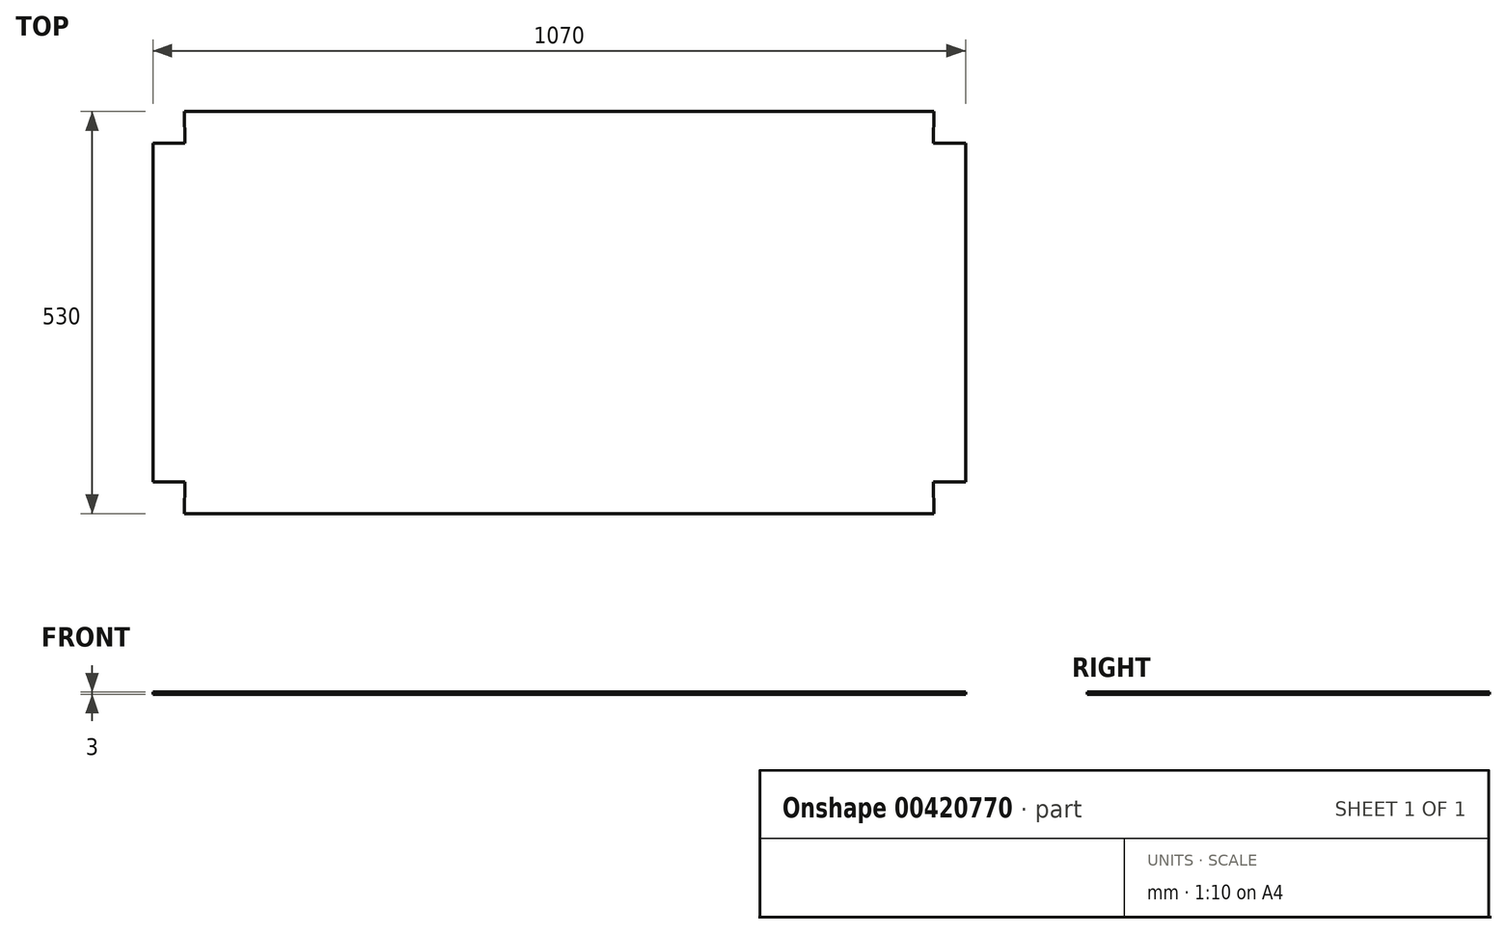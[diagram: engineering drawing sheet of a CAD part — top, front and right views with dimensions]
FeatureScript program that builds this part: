
annotation { "Feature Type Name" : "Feature", "Feature Type Description" : "" }
export const myFeature = defineFeature(function(context is Context, id is Id, definition is map)
    precondition{}
    {
        {
            var Q0;
            Q0=qCreatedBy(makeId("Top.planeOp"),FACE);
            var sketch = newSketch(context, id + "F0", { "sketchPlane" : qUnion([Q0])});
            skLineSegment(sketch, "E0.bottom", {"start": v(-882.96, -57.33) * mm, "end": v(104.05, -57.33) * mm});
            skLineSegment(sketch, "E0.top", {"start": v(-882.96, -587.33) * mm, "end": v(104.05, -587.33) * mm});
            skLineSegment(sketch, "E0.left", {"start": v(-924.45, -99.33) * mm, "end": v(-924.45, -545.33) * mm});
            skLineSegment(sketch, "E0.right", {"start": v(145.55, -99.33) * mm, "end": v(145.55, -545.33) * mm});
            skLineSegment(sketch, "E1.top", {"start": v(-924.45, -99.33) * mm, "end": v(-882.45, -99.33) * mm});
            skLineSegment(sketch, "E1.right", {"start": v(-882.96, -57.33) * mm, "end": v(-882.45, -99.33) * mm});
            skPoint(sketch, "E2", {"position": v(-389.45, -57.33) * mm});
            skPoint(sketch, "E3", {"position": v(-389.45, -587.33) * mm});
            skLineSegment(sketch, "E4", {"start": v(-389.45, -57.33) * mm, "end": v(-389.45, -587.33) * mm, "construction": true});
            skPoint(sketch, "E5", {"position": v(-924.45, -322.33) * mm});
            skPoint(sketch, "E6", {"position": v(145.55, -322.33) * mm});
            skLineSegment(sketch, "E7", {"start": v(-924.45, -322.33) * mm, "end": v(145.55, -322.33) * mm, "construction": true});
            skLineSegment(sketch, "E8.MirrorCS", {"start": v(104.05, -57.33) * mm, "end": v(103.55, -99.33) * mm});
            skLineSegment(sketch, "E9.MirrorCS", {"start": v(145.55, -99.33) * mm, "end": v(103.55, -99.33) * mm});
            skLineSegment(sketch, "E10.MirrorCS", {"start": v(-924.45, -545.33) * mm, "end": v(-882.45, -545.33) * mm});
            skLineSegment(sketch, "E11.MirrorCS", {"start": v(-882.96, -587.33) * mm, "end": v(-882.45, -545.33) * mm});
            skLineSegment(sketch, "E12.MirrorCS", {"start": v(145.55, -545.33) * mm, "end": v(103.55, -545.33) * mm});
            skLineSegment(sketch, "E13.MirrorCS", {"start": v(104.05, -587.33) * mm, "end": v(103.55, -545.33) * mm});
            skPoint(sketch, "E14.orphan", {"position": v(-924.45, -57.33) * mm});
            skPoint(sketch, "E15.orphan", {"position": v(-924.45, -587.33) * mm});
            skPoint(sketch, "E16.orphan", {"position": v(145.55, -587.33) * mm});
            skPoint(sketch, "E17.orphan", {"position": v(145.55, -57.33) * mm});
            skSolve(sketch);
        }
        {
            var Q0;
            Q0=qSketchRegion(id+"F0",true);
            extrude(context, id + "F1", {"entities" : qUnion([Q0]), "depth" : 3 * mm});
        }
    });
